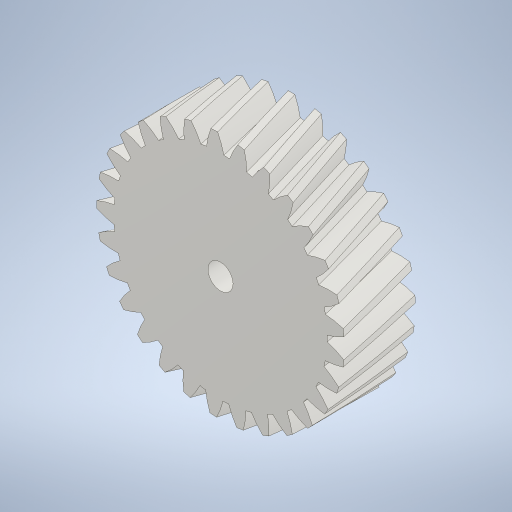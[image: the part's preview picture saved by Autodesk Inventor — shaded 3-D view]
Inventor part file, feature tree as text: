
AUTODESK INVENTOR PART (.ipt)
format: ipt  version: 2024.1 (Build 281209000, 209)  size: 608,768 bytes
history: native  units: mm (DEFAULTED — no unit token found)
features: plane x3, other x3, extrude x2, sketch x2
ambient origin geometry x8: Origin, YZ Plane, XZ Plane, XY Plane, X Axis, Y Axis, Z Axis, Center Point
bodies: Solid1 (feature_tree)
feature tree (10):
  extrude  "Extrusion1"  Depth=14.0mm TaperAngle=0.0deg
  plane  "Work Plane2"
  plane  "Work Plane8"
  plane  "Work Plane9"
  other  "Spur Gear"
  extrude  "Extrusion2"  Depth=10.0mm TaperAngle=0.0deg
  sketch  "Sketch1"  dims[d0=48.837039mm d1=14.0mm d2=0.0mm]
  other  "Srf1"
  sketch  "Sketch3"  dims[d3=45.034514mm d4=10.0mm d5=0.0mm d16=45.0mm d17=0.0mm d34=1.083308mm d39=0.0mm d41=0.0mm d43=45.0mm d46=45.0mm d47=0.0mm d48=0.0mm d49=4.96mm d50=0.0mm d51=0.0mm]
  other  "Pitch Diameter"
